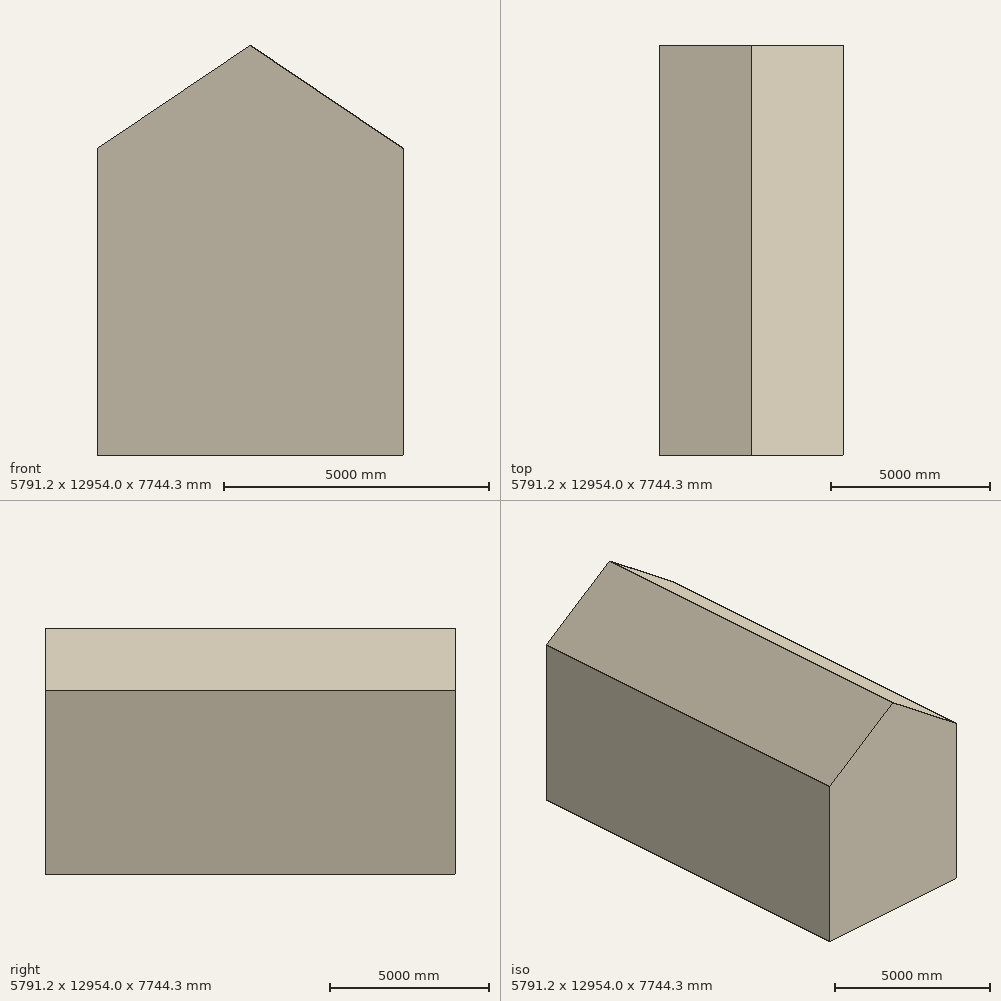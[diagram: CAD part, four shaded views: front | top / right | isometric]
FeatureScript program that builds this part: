
annotation { "Feature Type Name" : "Feature", "Feature Type Description" : "" }
export const myFeature = defineFeature(function(context is Context, id is Id, definition is map)
    precondition{}
    {
        {
            var Q0;
            Q0=qCreatedBy(makeId("Front.planeOp"),FACE);
            var sketch = newSketch(context, id + "F0", { "sketchPlane" : qUnion([Q0])});
            skLineSegment(sketch, "E0.bottom", {"start": v(-2895.6, 2248.84) * mm, "end": v(2895.6, 2248.84) * mm});
            skLineSegment(sketch, "E0.top", {"start": v(-2895.6, -3542.36) * mm, "end": v(2895.6, -3542.36) * mm});
            skLineSegment(sketch, "E0.left", {"start": v(-2895.6, 2248.84) * mm, "end": v(-2895.6, -3542.36) * mm});
            skLineSegment(sketch, "E0.right", {"start": v(2895.6, 2248.84) * mm, "end": v(2895.6, -3542.36) * mm});
            skLineSegment(sketch, "E1", {"start": v(-2895.6, 2248.84) * mm, "end": v(0, 4201.95) * mm});
            skLineSegment(sketch, "E2", {"start": v(0, 4201.95) * mm, "end": v(2895.6, 2248.84) * mm});
            skSolve(sketch);
        }
        {
            var Q0;
            Q0 = qSketchRegion(id + "F0", true);
            extrude(context, id + "F1", {"entities" : qUnion([Q0]), "endBound" : BoundingType.SYMMETRIC, "depth" : 12954 * mm});
        }
    });
